# Revit family: Faucet-Lavatory-KALLISTA-PER_SE-P26624_1
name_source: partatom
category: Plumbing Fixtures
units: mm (PartAtom-declared; Revit-internal decimal feet)

## family parameters
Cut with Voids When Loaded = No
Host = Face
Maintain Annotation Orientation = No
OmniClass Number = 23.31.11.00
OmniClass Title = Faucets
Part Type = Normal
Room Calculation Point = No
Round Connector Dimension = Use Diameter
Shared = No

## types (5) — shared parameters
ADA Compliant = No
Assembly Code = D2010
CW Connection = Yes
Cold Water Inlet = Cold Water Inlet
Date Modified = 07/04/2022
Default Elevation = 36"
Description = SINGLE CONTROL, TALL
Drain Included = Yes
Flow Rate = 1 GPM
HW Connection = Yes
Handle Clearance = 2 3/4"
Height = 8 5/8"
Hot Water Inlet = Hot Water Inlet
Length = 4 13/16"
Manufacturer = Kallista Co.
Master Format 2014 = 22 41 39
Master Format 2014 Name = Residential Faucets, Supplies, and Trim
Material = Premium Metal Construction
Pressure = 60.00 psi
Product Name = PER SE
Spout Reach = 4 13/16"
URL = https://www.kallista.com
Vent Connection = No
Waste Connection = No
Waste Water Outlet = Waste Water Outlet
WaterSense Certified = No
Width = 2 3/4"

## per-type parameters (varying)
| type | Finish | Model | Secondary Material | Type |
| AF-French Gold | Kallista-Metal-AF-French_Gold | P26624-00-AF | Kallista-Plastic-2MB-Vibrant_Brushed_Moderne_Brass | 1 |
| BAF-Brushed French Gold | Kallista-Metal-BAF-Brushed_French_Gold | P26624-00-BAF | Kallista-Plastic-2MB-Vibrant_Brushed_Moderne_Brass | 2 |
| BN-Brushed Nickel | Kallista-Metal-BN-Brushed_Nickel | P26624-00-BN | Kohler-Plastic-58-Thunder_Grey | 3 |
| CP-Chrome | Kallista-Metal-CP-Chrome | P26624-00-CP | Kohler-Plastic-58-Thunder_Grey | 4 |
| SN-Polished Nickel | Kallista-Metal-SN-Polished_Nickel | P26624-00-SN | Kohler-Plastic-58-Thunder_Grey | 5 |

## geometry (parser evidence)
native form markers: Sweep x5
no freeform markers — native parametric forms only
